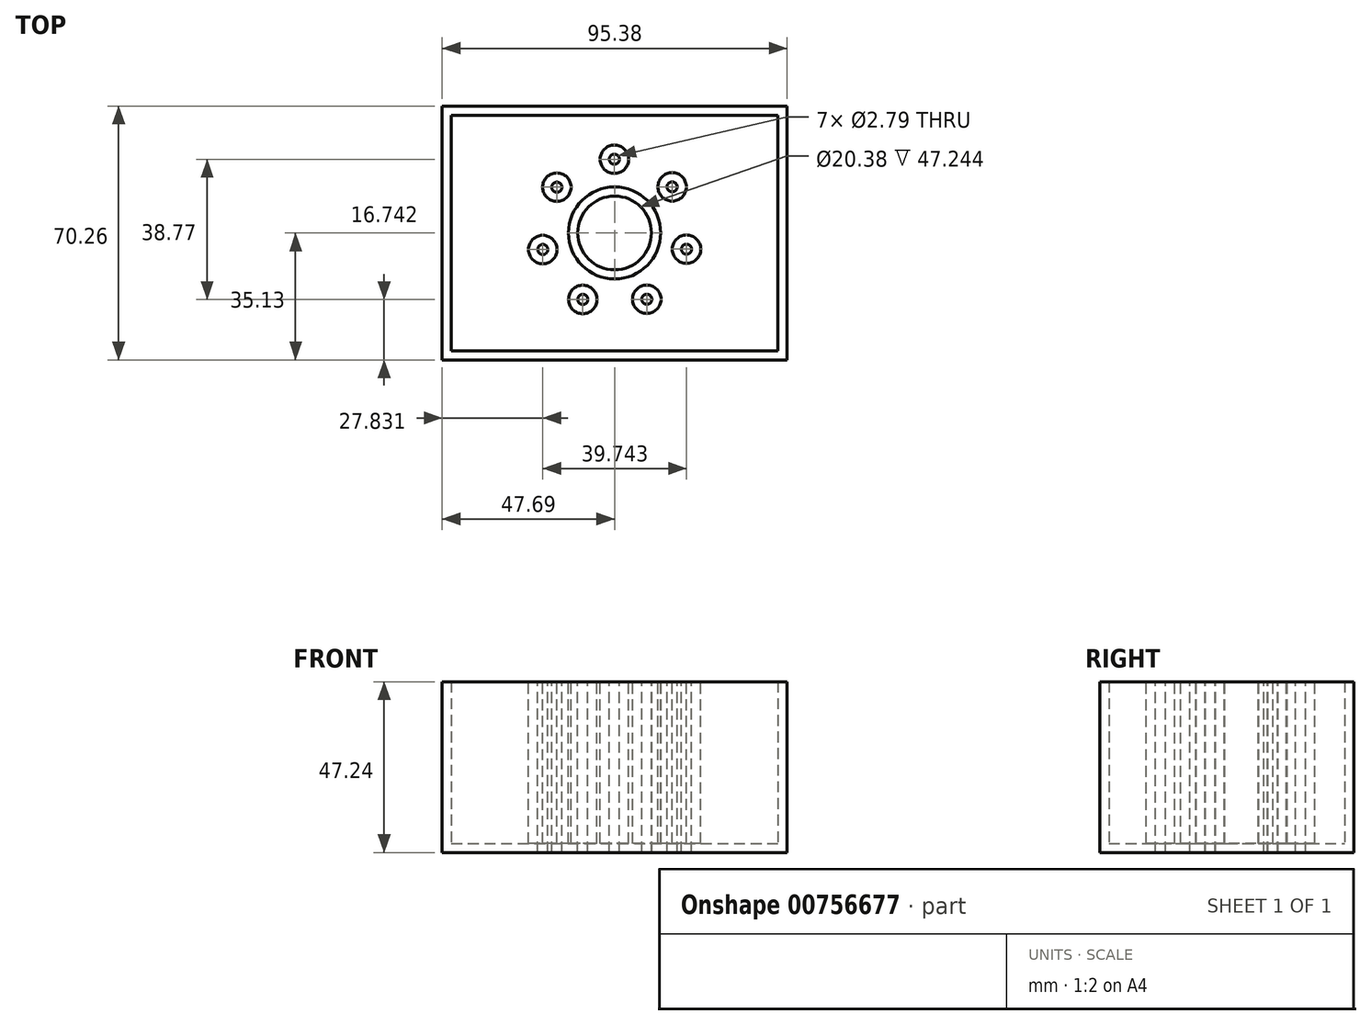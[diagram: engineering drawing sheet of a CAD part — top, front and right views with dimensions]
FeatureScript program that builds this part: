
annotation { "Feature Type Name" : "Feature", "Feature Type Description" : "" }
export const myFeature = defineFeature(function(context is Context, id is Id, definition is map)
    precondition{}
    {
        {
            var Q0;
            Q0=qCreatedBy(makeId("Top.planeOp"),FACE);
            var sketch = newSketch(context, id + "F0", { "sketchPlane" : qUnion([Q0])});
            skLineSegment(sketch, "E0.bottom", {"start": v(-47.7, -35.13) * mm, "end": v(47.7, -35.13) * mm});
            skLineSegment(sketch, "E0.top", {"start": v(-47.7, 35.13) * mm, "end": v(47.7, 35.13) * mm});
            skLineSegment(sketch, "E0.left", {"start": v(-47.7, -35.13) * mm, "end": v(-47.7, 35.13) * mm});
            skLineSegment(sketch, "E0.right", {"start": v(47.7, -35.13) * mm, "end": v(47.7, 35.13) * mm});
            skPoint(sketch, "E0.middle", {"position": v(0, 0) * mm});
            skSolve(sketch);
        }
        {
            var Q0;
            Q0 = qSketchRegion(id + "F0", true);
            extrude(context, id + "F1", {"entities" : qUnion([Q0]), "depth" : 47.24 * mm, "offsetDistance" : 25.4 * mm});
        }
        {
            var Q0;
            Q0=makeQuery(id+"F1.opExtrude","CAP_FACE",FACE,{"disambiguationData":[OSD([sQuery(id+"F0.wireOp",EDGE,"E0.bottom"),sQuery(id+"F0.wireOp",EDGE,"E0.top"),sQuery(id+"F0.wireOp",EDGE,"E0.left"),sQuery(id+"F0.wireOp",EDGE,"E0.right")])],"isStart":false});
            var sketch = newSketch(context, id + "F2", { "sketchPlane" : qUnion([Q0])});
            skCircle(sketch, "E1.cCircle", {"center": v(0, 0) * mm, "radius": 18.36 * mm, "construction": true});
            skLineSegment(sketch, "E1.0", {"start": v(19.88, -4.48) * mm, "end": v(8.9, -18.34) * mm});
            skLineSegment(sketch, "E1.1", {"start": v(8.9, -18.34) * mm, "end": v(-8.8, -18.39) * mm});
            skLineSegment(sketch, "E1.2", {"start": v(-8.8, -18.39) * mm, "end": v(-19.86, -4.59) * mm});
            skLineSegment(sketch, "E1.3", {"start": v(-19.86, -4.59) * mm, "end": v(-15.97, 12.66) * mm});
            skLineSegment(sketch, "E1.4", {"start": v(-15.97, 12.66) * mm, "end": v(-0.06, 20.38) * mm});
            skLineSegment(sketch, "E1.5", {"start": v(-0.06, 20.38) * mm, "end": v(15.9, 12.75) * mm});
            skLineSegment(sketch, "E1.6", {"start": v(15.9, 12.75) * mm, "end": v(19.88, -4.48) * mm});
            skPoint(sketch, "E1.0.midPoint", {"position": v(14.39, -11.41) * mm});
            skSolve(sketch);
        }
        {
            var Q0;
            Q0=sQuery(id+"F2.wireOp",VERTEX,"E1.5.start");
            var Q1;
            Q1=sQuery(id+"F2.wireOp",VERTEX,"E1.4.start");
            var Q2;
            Q2=sQuery(id+"F2.wireOp",VERTEX,"E1.3.start");
            var Q3;
            Q3=sQuery(id+"F2.wireOp",VERTEX,"E1.2.start");
            var Q4;
            Q4=sQuery(id+"F2.wireOp",VERTEX,"E1.1.start");
            var Q5;
            Q5=sQuery(id+"F2.wireOp",VERTEX,"E1.6.end");
            var Q6;
            Q6=sQuery(id+"F2.wireOp",VERTEX,"E1.6.start");
            var Q7;
            Q7=makeQuery(id+"F1.opExtrude","SWEPT_BODY",BODY,{"disambiguationData":[OSD([sQuery(id+"F0.wireOp",EDGE,"E0.bottom"),sQuery(id+"F0.wireOp",EDGE,"E0.top"),sQuery(id+"F0.wireOp",EDGE,"E0.left"),sQuery(id+"F0.wireOp",EDGE,"E0.right")])]});
            hole(context, id + "F3", {"style" : HoleStyle.SIMPLE, "endStyle" : HoleEndStyle.THROUGH, "standardTappedOrClearance" : lookupTablePath({ "standard" : "ANSI", "fit" : "Normal (ASME)", "size" : "#3", "type" : "Clearance" }), "standardBlindInLast" : lookupTablePath({ "fit" : "Free", "standard" : "ANSI", "size" : "#3", "type" : "Clearance" }), "holeDiameter" : 2.8 * mm, "majorDiameter" : 6.35 * mm, "isTappedThrough" : true, "tappedDepth" : 12.7 * mm, "tapClearance" : 3, "locations" : qUnion([Q0, Q1, Q2, Q3, Q4, Q5, Q6]), "scope" : qUnion([Q7])});
        }
        {
            var Q0;
            Q0=makeQuery(id+"F1.opExtrude","CAP_FACE",FACE,{"disambiguationData":[OSD([sQuery(id+"F0.wireOp",EDGE,"E0.bottom"),sQuery(id+"F0.wireOp",EDGE,"E0.top"),sQuery(id+"F0.wireOp",EDGE,"E0.left"),sQuery(id+"F0.wireOp",EDGE,"E0.right")])],"isStart":false});
            var sketch = newSketch(context, id + "F4", { "sketchPlane" : qUnion([Q0])});
            skCircle(sketch, "E2", {"center": v(0, 0) * mm, "radius": 10.2 * mm});
            skSolve(sketch);
        }
        {
            var Q0;
            Q0=makeQuery(id+"F4.imprint","IMPRINT",FACE,{"disambiguationData":[TD([[makeQuery(id+"F4.imprint","IMPRINT",EDGE,{"derivedFrom":sQuery(id+"F4.wireOp",EDGE,"E2")}),1.0]])]});
            extrude(context, id + "F5", {"entities" : qUnion([Q0]), "operationType" : NewBodyOperationType.REMOVE, "endBound" : BoundingType.UP_TO_NEXT, "oppositeDirection" : true, "depth" : 25.4 * mm, "offsetDistance" : 25.4 * mm});
        }
        {
            var Q0;
            Q0=makeQuery(id+"F1.opExtrude","CAP_FACE",FACE,{"disambiguationData":[OSD([sQuery(id+"F0.wireOp",EDGE,"E0.bottom"),sQuery(id+"F0.wireOp",EDGE,"E0.top"),sQuery(id+"F0.wireOp",EDGE,"E0.left"),sQuery(id+"F0.wireOp",EDGE,"E0.right")])],"isStart":false});
            shell(context, id + "F6", {"entities" : qUnion([Q0]), "thickness" : 2.54 * mm});
        }
    });
